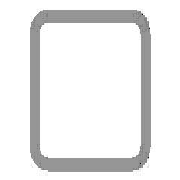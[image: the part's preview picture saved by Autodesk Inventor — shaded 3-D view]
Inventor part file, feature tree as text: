
AUTODESK INVENTOR PART (.ipt)
format: ipt  version: 2024 (Build 280153000, 153)  size: 129,024 bytes
history: native  units: mm (DEFAULTED — no unit token found)
features: other x4, extrude x1, sketch x1, plane x1
ambient origin geometry x8: Origin, YZ Plane, XZ Plane, XY Plane, X Axis, Y Axis, Z Axis, Center Point
bodies: Solid1 (feature_tree)
feature tree (7):
  parser-record x1  (decoder bookkeeping rows leaked as tree rows — omitted from the tree; the rows remain in map.json)
  other  "Driven Length"
  other  "Plano inicial"
  other  "Plano final"
  extrude  "Cuerpo"  TaperAngle=0.0deg  [1 undecoded]
  sketch  "Sketch3"  dims[d3=230.0mm d4=0.0mm d10=50.8mm d11=50.8mm d12=3.175mm d13=-0.0mm d14=230.0mm d15=25.4mm d16=25.4mm d17=6.35mm d18=90.0deg d19=230.0mm]
  plane  "Work Plane3"
note: 1 required parameter value undecoded (feature->parameter linkage not recoverable at this tier; creation-order binding heuristic only, values carry confidence <= 0.55)
